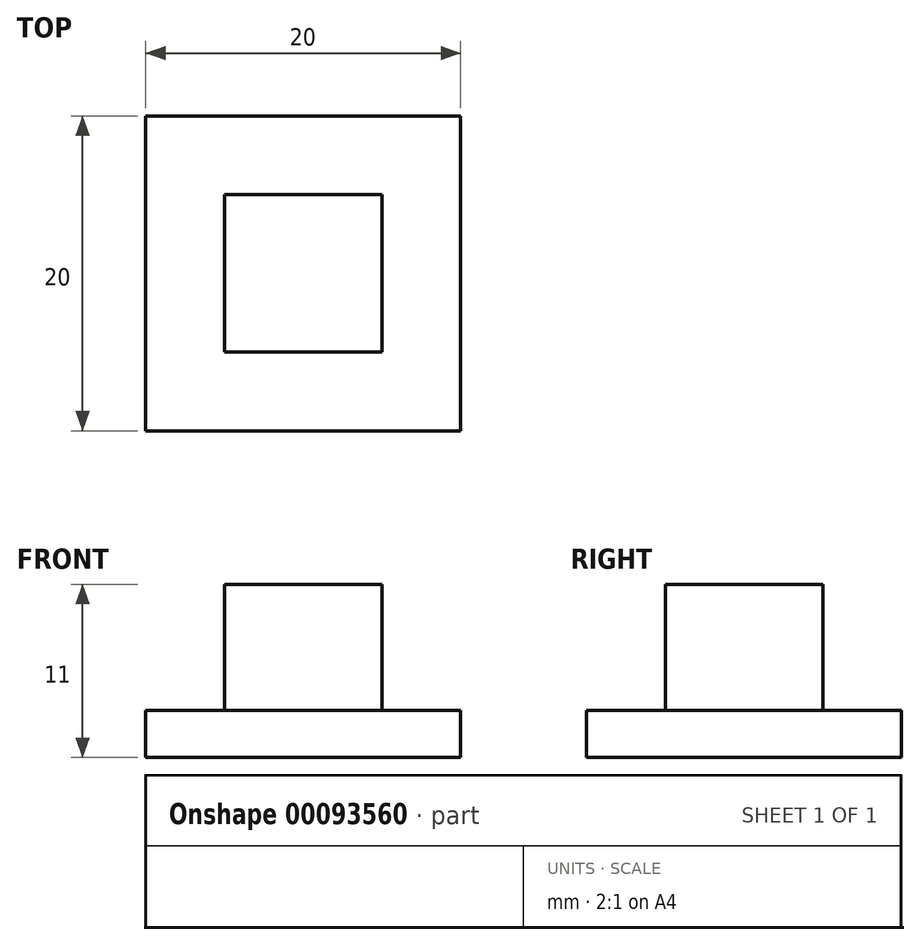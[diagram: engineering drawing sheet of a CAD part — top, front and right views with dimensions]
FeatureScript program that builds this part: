
annotation { "Feature Type Name" : "Feature", "Feature Type Description" : "" }
export const myFeature = defineFeature(function(context is Context, id is Id, definition is map)
    precondition{}
    {
        {
            var Q0;
            Q0=qCreatedBy(makeId("Top.planeOp"),FACE);
            var sketch = newSketch(context, id + "F0", { "sketchPlane" : qUnion([Q0])});
            skLineSegment(sketch, "E0.bottom", {"start": v(10, -10) * mm, "end": v(-10, -10) * mm});
            skLineSegment(sketch, "E0.top", {"start": v(10, 10) * mm, "end": v(-10, 10) * mm});
            skLineSegment(sketch, "E0.left", {"start": v(10, -10) * mm, "end": v(10, 10) * mm});
            skLineSegment(sketch, "E0.right", {"start": v(-10, -10) * mm, "end": v(-10, 10) * mm});
            skPoint(sketch, "E0.middle", {"position": v(0, 0) * mm});
            skSolve(sketch);
        }
        {
            var Q0;
            Q0 = qSketchRegion(id + "F0", true);
            extrude(context, id + "F1", {"entities" : qUnion([Q0]), "depth" : 3 * mm});
        }
        {
            var Q0;
            Q0=makeQuery(id+"F1.opExtrude","CAP_FACE",FACE,{"disambiguationData":[OSD([sQuery(id+"F0.wireOp",EDGE,"E0.bottom"),sQuery(id+"F0.wireOp",EDGE,"E0.top"),sQuery(id+"F0.wireOp",EDGE,"E0.left"),sQuery(id+"F0.wireOp",EDGE,"E0.right")])],"isStart":false});
            var sketch = newSketch(context, id + "F2", { "sketchPlane" : qUnion([Q0])});
            skLineSegment(sketch, "E1.bottom", {"start": v(5, -5) * mm, "end": v(-5, -5) * mm});
            skLineSegment(sketch, "E1.top", {"start": v(5, 5) * mm, "end": v(-5, 5) * mm});
            skLineSegment(sketch, "E1.left", {"start": v(5, -5) * mm, "end": v(5, 5) * mm});
            skLineSegment(sketch, "E1.right", {"start": v(-5, -5) * mm, "end": v(-5, 5) * mm});
            skPoint(sketch, "E1.middle", {"position": v(0, 0) * mm});
            skSolve(sketch);
        }
        {
            var Q0;
            Q0 = qSketchRegion(id + "F2", true);
            extrude(context, id + "F3", {"entities" : qUnion([Q0]), "operationType" : NewBodyOperationType.ADD, "depth" : 8 * mm});
        }
    });
